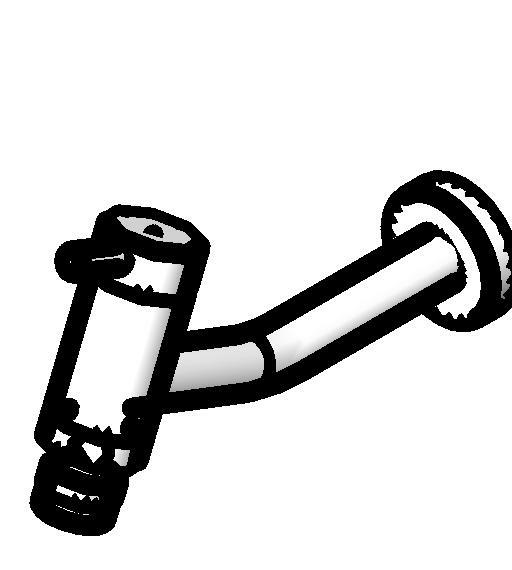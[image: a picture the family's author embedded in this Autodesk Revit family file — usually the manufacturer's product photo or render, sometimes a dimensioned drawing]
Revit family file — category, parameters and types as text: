
# Revit family: Deca_Torneira Cozinha Link_1159.C.LNK_ Bica Móvel Curta Parede
name_source: partatom
category: Plumbing Fixtures
revit_build: Autodesk Revit Architecture 2012 (Build: 20120126_0600(x64)
units: mm (PartAtom-declared; Revit-internal decimal feet)

## types (1)
- 1159.C.LNK_Cromado CR10
    Aprovado por = Contino/quattroD
    Assembly Code = D2020
    Atendimento ao Cliente = 0800-011-7073
    CWFU = 0
    Consumo = Varia com a pressão
    Criado por = Contino/quattroD
    Código = 1159.C.LNK
    Default Elevation = 800 mm  [stored 2.62467 ft]
    Description = Torneira Cozinha parede
    Diâmetro Água Fria = 15 mm  [stored 0.0492126 ft]
    Flow Pressure = 0.00 psi
    HWFU = 0
    Informações Complementares = Mecanismo: 1/4 de volta
    Linha = Link
    Louça/Metais = Metal
    Manufacturer = Deca
    Material = Deca_Latão Cromado e Plástico de Engenharia
    Model = 1159.C.LNK
    Norma = ABNT NBR 10281: 2003
    Peso Liquido (Kg) = 0.62
    Pressão = 2 A 40 mca
    Produto = Torneira Cozinha bica móvel curta Parede
    Raio Água Fria = 8 mm  [stored 0.0262467 ft]
    Segmento = Competitivo
    Torneira = Deca CR10 Cromado Metal
    URL = www.deca.com.br/produtos
    Variações de COR = Cromado (1159.C.LNK).
    WFU = 0

note: [stored X ft] marks values corroborated as IEEE doubles in the binary element streams (Revit-internal decimal feet)

## geometry (parser evidence)
native form markers: Blend x4, Sweep x3
no freeform markers — native parametric forms only
